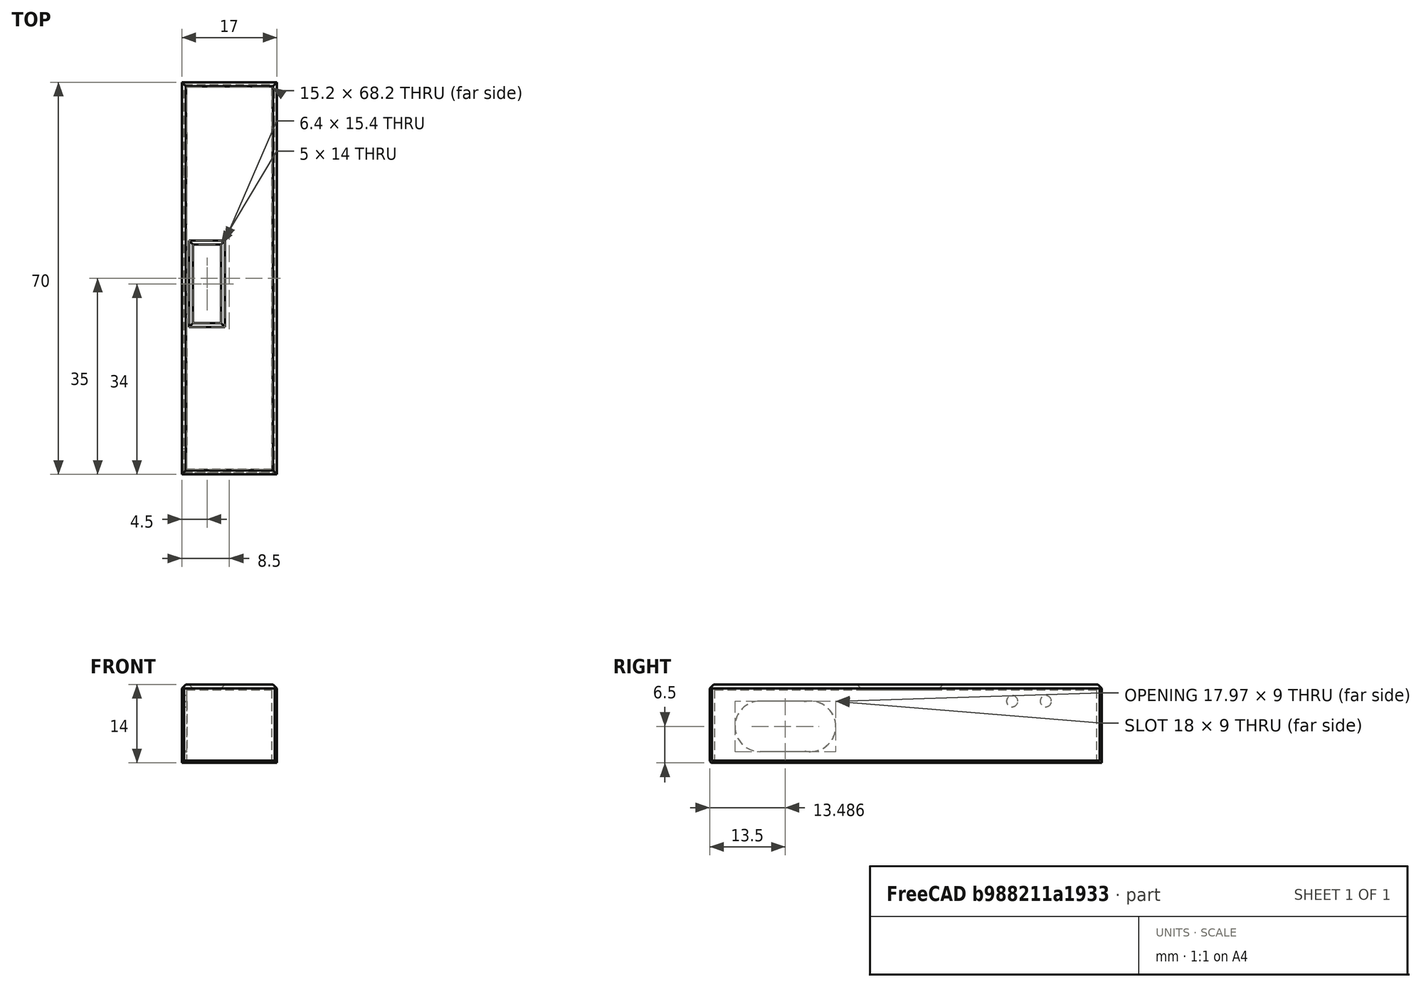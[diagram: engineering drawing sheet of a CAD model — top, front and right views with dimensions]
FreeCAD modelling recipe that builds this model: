
FCSTD DOCUMENT  (FreeCAD 0.20R29410 (Git))
Label: RTO_Cart_CUP
License: All rights reserved
LicenseURL: http://en.wikipedia.org/wiki/All_rights_reserved
objects: Part::Cut×7, Part::Chamfer×6, Part::Box×5, Part::Cylinder×4, Part::MultiFuse×1, Mesh::Feature×1, Part::Feature×1
note: 24 computed .brp shape members not serialized (recipe doc carries the construction recipe); baked Part::Feature solids carry a one-line shape summary decoded from their .brp

FEATURE [Part::Box] Box  label="foroSlot"
  AttacherType = Attacher::AttachEngine3D
  Height = 18
  Length = 15.2
  Placement = pos=(-0.1,-0.1,-9) rot=(0,0,1;0rad)
  Width = 68.2
FEATURE [Part::Box] Box001  label="Cubo"
  AttacherType = Attacher::AttachEngine3D
  Height = 14
  Length = 17
  Placement = pos=(-1,-1,-4) rot=(0,0,1;0rad)
  Width = 70
FEATURE [Part::Cut] Cut
  Base = -> Box001
  Tool = -> Box
FEATURE [Part::Box] Box002  label="Cubo001"
  AttacherType = Attacher::AttachEngine3D
  Height = 11
  Length = 5
  Placement = pos=(1,26,2) rot=(0,0,1;0rad)
  Width = 14
FEATURE [Part::Cut] Cut001
  Base = -> Cut
  Tool = -> Box002
FEATURE [Part::Chamfer] Chamfer
  Base = -> Cut001
  Edges = 4 edges r=0.7: [Edge10,Edge11,Edge12,Edge13]
FEATURE [Part::Chamfer] Chamfer001
  Base = -> Chamfer
  Edges = 4 edges r=0.7: [Edge5,Edge6,Edge7,Edge8]
FEATURE [Part::Cylinder] Cylinder  label="Led1"
  Angle = 360
  AttacherType = Attacher::AttachEngine3D
  FirstAngle = 0
  Height = 10
  Placement = pos=(-5,59,7) rot=(0,1,0;1.5708rad)
  Radius = 1
  SecondAngle = 0
FEATURE [Part::Cylinder] Cylinder001  label="Cilindro"
  Angle = 360
  AttacherType = Attacher::AttachEngine3D
  FirstAngle = 0
  Height = 10
  Placement = pos=(-5,53,7) rot=(0,1,0;1.5708rad)
  Radius = 1
  SecondAngle = 0
FEATURE [Part::Cylinder] Cylinder002  label="Cilindro001"
  Angle = 360
  AttacherType = Attacher::AttachEngine3D
  FirstAngle = 0
  Height = 12
  Placement = pos=(-8,8,2.5) rot=(0,1,0;1.5708rad)
  Radius = 4.5
  SecondAngle = 0
FEATURE [Part::Cylinder] Cylinder003  label="Cilindro002"
  Angle = 360
  AttacherType = Attacher::AttachEngine3D
  FirstAngle = 0
  Height = 12
  Placement = pos=(-8,17,2.5) rot=(0,1,0;1.5708rad)
  Radius = 4.5
  SecondAngle = 0
FEATURE [Part::MultiFuse] Fusion
  Shapes = -> [Cylinder003,Cylinder002]
FEATURE [Part::Cut] Cut002
  Base = -> Chamfer001
  Tool = -> Fusion
FEATURE [Part::Cut] Cut003
  Base = -> Cut002
  Tool = -> Cylinder001
FEATURE [Part::Cut] Cut004
  Base = -> Cut003
  Tool = -> Cylinder
FEATURE [Part::Chamfer] Chamfer002
  Base = -> Cut004
  Edges = 2 edges r=0.4: [Edge35,Edge38]
FEATURE [Part::Chamfer] Chamfer003
  Base = -> Chamfer002
  Edges = 2 edges r=0.4: [Edge3,Edge22]
FEATURE [Part::Chamfer] Chamfer004
  Base = -> Chamfer003
  Edges = 4 edges r=0.4: [Edge2,Edge4,Edge14,Edge17]
FEATURE [Part::Box] Box003  label="Cubo002"
  AttacherType = Attacher::AttachEngine3D
  Height = 9
  Length = 12
  Placement = pos=(-8,8,-2) rot=(0,0,1;0rad)
  Width = 9
FEATURE [Part::Cut] Cut005
  Base = -> Cut002
  Tool = -> Box003
FEATURE [Part::Chamfer] Chamfer005
  Base = -> Cut005
  Edges = 1 edges r=0.3: [Edge33]
FEATURE [Part::Box] Box004  label="Cubo003"
  AttacherType = Attacher::AttachEngine3D
  Height = 9
  Length = 8
  Placement = pos=(-5,8,-2) rot=(0,0,1;0rad)
  Width = 8
FEATURE [Part::Cut] Cut006
  Base = -> Chamfer004
  Tool = -> Box004
FEATURE [Mesh::Feature] Mesh  label="Cut006 (Meshed)"
FEATURE [Part::Feature] Refined_Mesh_Solid_77090
  shape: bbox 17 x 70 x 14 mm, 123 faces, 0 solids (baked)
